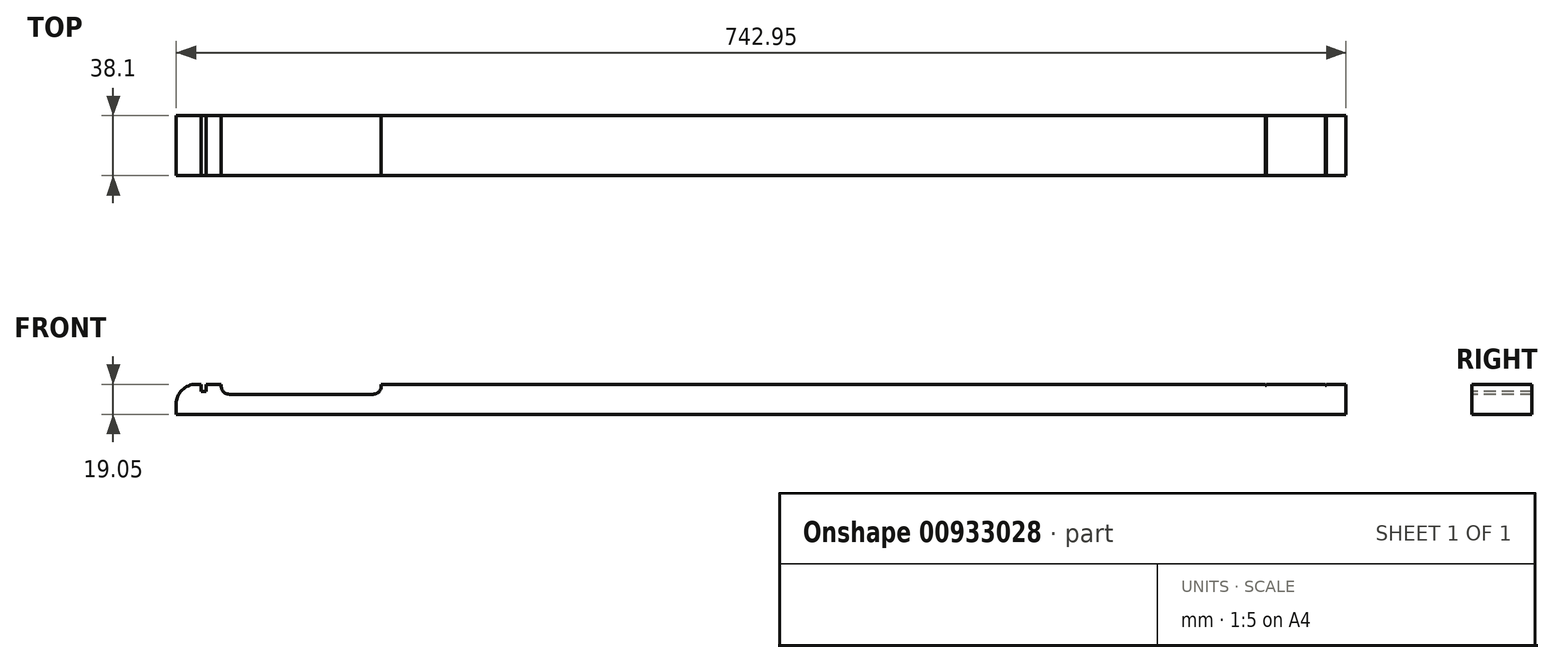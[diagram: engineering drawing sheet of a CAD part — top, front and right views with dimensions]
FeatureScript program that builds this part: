
annotation { "Feature Type Name" : "Feature", "Feature Type Description" : "" }
export const myFeature = defineFeature(function(context is Context, id is Id, definition is map)
    precondition{}
    {
        {
            var Q0;
            Q0=qCreatedBy(makeId("Right.planeOp"),FACE);
            cPlane(context, id + "F7", {"entities" : qUnion([Q0]), "cplaneType" : CPlaneType.OFFSET, "offset" : 711.2 * mm, "oppositeDirection" : true, "width" : 152.4 * mm, "height" : 152.4 * mm});
        }
        {
            var Q0;
            Q0=qCreatedBy(makeId("Top.planeOp"),FACE);
            var sketch = newSketch(context, id + "F8", { "sketchPlane" : qUnion([Q0])});
            skLineSegment(sketch, "E0.bottom", {"start": v(-730.25, -19.05) * mm, "end": v(12.7, -19.05) * mm});
            skLineSegment(sketch, "E0.top", {"start": v(-730.25, 19.05) * mm, "end": v(12.7, 19.05) * mm});
            skLineSegment(sketch, "E0.left", {"start": v(-730.25, -19.05) * mm, "end": v(-730.25, 19.05) * mm});
            skLineSegment(sketch, "E0.right", {"start": v(12.7, -19.05) * mm, "end": v(12.7, 19.05) * mm});
            skPoint(sketch, "E1", {"position": v(12.7, 0) * mm});
            skPoint(sketch, "E2", {"position": v(-711.2, 0) * mm});
            skSolve(sketch);
        }
        {
            var Q0;
            Q0=qSketchRegion(id+"F8",true);
            extrude(context, id + "F0", {"entities" : qUnion([Q0]), "depth" : 19.05 * mm});
        }
        {
            var Q0;
            Q0=qCreatedBy(makeId("Front.planeOp"),FACE);
            var sketch = newSketch(context, id + "F1", { "sketchPlane" : qUnion([Q0])});
            skLineSegment(sketch, "E3.bottom", {"start": v(-0.38, 19.05) * mm, "end": v(0.38, 19.05) * mm});
            skLineSegment(sketch, "E3.top", {"start": v(-0.38, 18.29) * mm, "end": v(0.38, 18.29) * mm});
            skLineSegment(sketch, "E3.left", {"start": v(-0.38, 19.05) * mm, "end": v(-0.38, 18.29) * mm});
            skLineSegment(sketch, "E3.right", {"start": v(0.38, 19.05) * mm, "end": v(0.38, 18.29) * mm});
            skPoint(sketch, "E4", {"position": v(0, 19.05) * mm});
            skSolve(sketch);
        }
        {
            var Q0;
            Q0=qSketchRegion(id+"F1",true);
            extrude(context, id + "F2", {"entities" : qUnion([Q0]), "operationType" : NewBodyOperationType.REMOVE, "endBound" : BoundingType.THROUGH_ALL, "oppositeDirection" : true, "depth" : 25.4 * mm, "hasSecondDirection" : true, "secondDirectionBound" : SecondDirectionBoundingType.THROUGH_ALL, "secondDirectionOppositeDirection" : false, "secondDirectionDepth" : 25.4 * mm});
        }
        {
            var Q0;
            Q0=qCreatedBy(makeId("Front.planeOp"),FACE);
            var sketch = newSketch(context, id + "F3", { "sketchPlane" : qUnion([Q0])});
            skLineSegment(sketch, "E5.bottom", {"start": v(-38.48, 19.05) * mm, "end": v(-37.72, 19.05) * mm});
            skLineSegment(sketch, "E5.top", {"start": v(-38.48, 18.29) * mm, "end": v(-37.72, 18.29) * mm});
            skLineSegment(sketch, "E5.left", {"start": v(-38.48, 19.05) * mm, "end": v(-38.48, 18.29) * mm});
            skLineSegment(sketch, "E5.right", {"start": v(-37.72, 19.05) * mm, "end": v(-37.72, 18.29) * mm});
            skPoint(sketch, "E6", {"position": v(-38.1, 19.05) * mm});
            skPoint(sketch, "E7", {"position": v(0.38, 19.05) * mm});
            skSolve(sketch);
        }
        {
            var Q0;
            Q0=qSketchRegion(id+"F3",true);
            extrude(context, id + "F9", {"entities" : qUnion([Q0]), "operationType" : NewBodyOperationType.REMOVE, "endBound" : BoundingType.THROUGH_ALL, "oppositeDirection" : true, "depth" : 25.4 * mm, "hasSecondDirection" : true, "secondDirectionBound" : SecondDirectionBoundingType.THROUGH_ALL, "secondDirectionOppositeDirection" : false, "secondDirectionDepth" : 25.4 * mm});
        }
        {
            var Q0;
            Q0=qCreatedBy(makeId("Front.planeOp"),FACE);
            var sketch = newSketch(context, id + "F10", { "sketchPlane" : qUnion([Q0])});
            skLineSegment(sketch, "E8.bottom", {"start": v(-600.08, 19.05) * mm, "end": v(-701.68, 19.05) * mm});
            skLineSegment(sketch, "E8.top", {"start": v(-605.15, 12.7) * mm, "end": v(-696.6, 12.7) * mm});
            skLineSegment(sketch, "E8.left", {"start": v(-600.08, 19.05) * mm, "end": v(-600.08, 17.78) * mm});
            skLineSegment(sketch, "E8.right", {"start": v(-701.68, 19.05) * mm, "end": v(-701.68, 17.78) * mm});
            skPoint(sketch, "E9.visualSharp", {"position": v(-701.68, 12.7) * mm});
            skArc(sketch, "E9.filletArc", {"start": v(-701.68, 17.78) * mm, "mid": v(-700.19, 14.19) * mm, "end": v(-696.6, 12.7) * mm});
            skPoint(sketch, "E10.visualSharp", {"position": v(-600.08, 12.7) * mm});
            skArc(sketch, "E10.filletArc", {"start": v(-605.15, 12.7) * mm, "mid": v(-601.56, 14.19) * mm, "end": v(-600.08, 17.78) * mm});
            skPoint(sketch, "E11", {"position": v(-711.2, 19.05) * mm});
            skSolve(sketch);
        }
        {
            var Q0;
            Q0=qSketchRegion(id+"F10",true);
            extrude(context, id + "F11", {"entities" : qUnion([Q0]), "operationType" : NewBodyOperationType.REMOVE, "endBound" : BoundingType.THROUGH_ALL, "oppositeDirection" : true, "depth" : 25.4 * mm, "hasSecondDirection" : true, "secondDirectionBound" : SecondDirectionBoundingType.THROUGH_ALL, "secondDirectionOppositeDirection" : false, "secondDirectionDepth" : 25.4 * mm});
        }
        {
            var Q0;
            Q0=qCreatedBy(makeId("Front.planeOp"),FACE);
            var sketch = newSketch(context, id + "F12", { "sketchPlane" : qUnion([Q0])});
            skLineSegment(sketch, "E12.bottom", {"start": v(-711.2, 19.05) * mm, "end": v(-714.38, 19.05) * mm});
            skLineSegment(sketch, "E12.top", {"start": v(-711.2, 14.48) * mm, "end": v(-714.38, 14.48) * mm});
            skLineSegment(sketch, "E12.left", {"start": v(-711.2, 19.05) * mm, "end": v(-711.2, 14.48) * mm});
            skLineSegment(sketch, "E12.right", {"start": v(-714.38, 19.05) * mm, "end": v(-714.38, 14.48) * mm});
            skSolve(sketch);
        }
        {
            var Q0;
            Q0=qSketchRegion(id+"F12",true);
            extrude(context, id + "F4", {"entities" : qUnion([Q0]), "operationType" : NewBodyOperationType.REMOVE, "endBound" : BoundingType.THROUGH_ALL, "oppositeDirection" : true, "depth" : 25.4 * mm, "hasSecondDirection" : true, "secondDirectionBound" : SecondDirectionBoundingType.THROUGH_ALL, "secondDirectionOppositeDirection" : false, "secondDirectionDepth" : 25.4 * mm});
        }
        {
            var Q0;
            Q0=makeQuery(id+"F0.opExtrude","CAP_EDGE",EDGE,{"disambiguationData":[OSD([sQuery(id+"F8.wireOp",EDGE,"E0.left")])],"isStart":false});
            fillet(context, id + "F5", {"entities" : qUnion([Q0]), "radius" : 12.7 * mm, "tangentPropagation" : true, "allowEdgeOverflow" : false});
        }
    });
